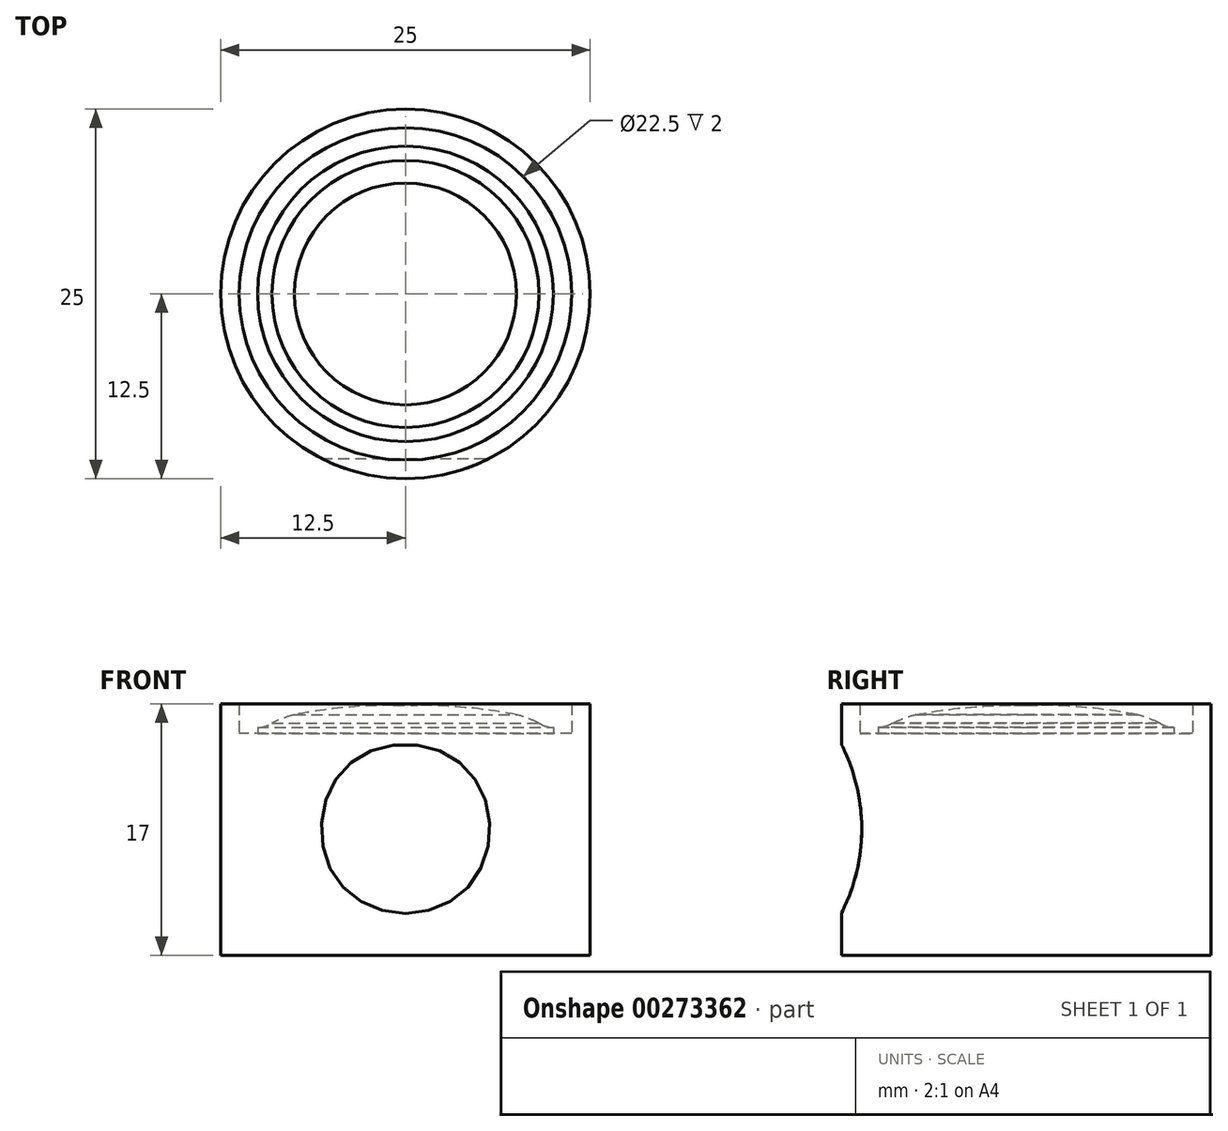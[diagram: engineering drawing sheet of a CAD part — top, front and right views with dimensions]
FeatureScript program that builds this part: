
annotation { "Feature Type Name" : "Feature", "Feature Type Description" : "" }
export const myFeature = defineFeature(function(context is Context, id is Id, definition is map)
    precondition{}
    {
        {
            var Q0;
            Q0=qCreatedBy(makeId("Front.planeOp"),FACE);
            var sketch = newSketch(context, id + "F0", { "sketchPlane" : qUnion([Q0])});
            skLineSegment(sketch, "E0", {"start": v(4.98, -0.38) * mm, "end": v(4.98, 1.12) * mm});
            skLineSegment(sketch, "E1", {"start": v(4.98, 1.12) * mm, "end": v(4.18, 1.12) * mm});
            skLineSegment(sketch, "E2", {"start": v(4.98, -0.38) * mm, "end": v(4.98, -0.79) * mm});
            skLineSegment(sketch, "E3", {"start": v(-6.42, -0.38) * mm, "end": v(-5.02, -0.38) * mm, "construction": true});
            skLineSegment(sketch, "E4", {"start": v(4.98, -0.79) * mm, "end": v(-5.02, -0.79) * mm});
            skLineSegment(sketch, "E5", {"start": v(-5.02, -0.79) * mm, "end": v(-5.02, -0.38) * mm});
            skArc(sketch, "E6", {"start": v(4.18, 1.12) * mm, "mid": v(0.81, 0.96) * mm, "end": v(-2.53, 0.49) * mm});
            skArc(sketch, "E7", {"start": v(-5.02, -0.38) * mm, "mid": v(-4.51, -0.3) * mm, "end": v(-4.05, -0.08) * mm});
            skArc(sketch, "E8", {"start": v(-2.53, 0.49) * mm, "mid": v(-3.3, 0.24) * mm, "end": v(-4.05, -0.08) * mm});
            skSolve(sketch);
        }
        {
            var Q0;
            Q0=makeQuery(id+"F0.imprint","IMPRINT",FACE,{"disambiguationData":[TD([[makeQuery(id+"F0.imprint","IMPRINT",EDGE,{"derivedFrom":sQuery(id+"F0.wireOp",EDGE,"E0")}),1.0]])]});
            var Q1;
            Q1=sQuery(id+"F0.wireOp",EDGE,"E0");
            revolve(context, id + "F1", {"entities" : qUnion([Q0]), "axis" : qUnion([Q1]), "revolveType" : RevolveType.FULL});
        }
        {
            var Q0;
            Q0=makeQuery(id+"F1.opRevolve","SWEPT_FACE",FACE,{"disambiguationData":[OSD([sQuery(id+"F0.wireOp",EDGE,"E4")])]});
            var sketch = newSketch(context, id + "F2", { "sketchPlane" : qUnion([Q0])});
            skCircle(sketch, "E9", {"center": v(4.98, 0) * mm, "radius": 12.5 * mm});
            skSolve(sketch);
        }
        {
            var Q0;
            Q0=makeQuery(id+"F2.imprint","IMPRINT",FACE,{"disambiguationData":[TD([[makeQuery(id+"F2.imprint","IMPRINT",EDGE,{"derivedFrom":sQuery(id+"F2.wireOp",EDGE,"E9")}),1.0]])]});
            var Q1;
            Q1=makeQuery(id+"F2.imprint","IMPRINT",FACE,{"disambiguationData":[TD([[makeQuery(id+"F2.imprint","IMPRINT",EDGE,{"derivedFrom":makeQuery(id+"F1.opRevolve","SWEPT_EDGE",EDGE,{"disambiguationData":[OSD([sQuery(id+"F0.wireOp",EDGE,"E4"),sQuery(id+"F0.wireOp",EDGE,"E5")])]})}),1.0]])]});
            extrude(context, id + "F3", {"entities" : qUnion([Q0, Q1]), "operationType" : NewBodyOperationType.ADD, "depth" : 15 * mm, "offsetDistance" : 25 * mm});
        }
        {
            var Q0;
            Q0=makeQuery(id+"F3.opExtrude","CAP_FACE",FACE,{"disambiguationData":[OSD([sQuery(id+"F2.wireOp",EDGE,"E9")])],"isStart":true});
            var sketch = newSketch(context, id + "F4", { "sketchPlane" : qUnion([Q0])});
            skCircle(sketch, "E10", {"center": v(4.98, 0) * mm, "radius": 11.25 * mm});
            skSolve(sketch);
        }
        {
            var Q0;
            Q0=makeQuery(id+"F4.imprint","IMPRINT",FACE,{"disambiguationData":[TD([[makeQuery(id+"F4.imprint","IMPRINT",EDGE,{"derivedFrom":sQuery(id+"F4.wireOp",EDGE,"E10")}),-1.0]])]});
            extrude(context, id + "F5", {"entities" : qUnion([Q0]), "operationType" : NewBodyOperationType.ADD, "depth" : 2 * mm, "offsetDistance" : 25 * mm});
        }
        {
            var Q0;
            Q0=qCreatedBy(makeId("Right.planeOp"),FACE);
            cPlane(context, id + "F6", {"entities" : qUnion([Q0]), "cplaneType" : CPlaneType.OFFSET, "offset" : 17.3 * mm, "width" : 150 * mm, "height" : 150 * mm});
        }
        {
            var Q0;
            Q0=qCreatedBy(id+"F6.planeOp",FACE);
            var sketch = newSketch(context, id + "F7", { "sketchPlane" : qUnion([Q0])});
            skLineSegment(sketch, "E11", {"start": v(-13.47, 2.71) * mm, "end": v(0, 2.71) * mm, "construction": true});
            skLineSegment(sketch, "E12", {"start": v(0, 1.27) * mm, "end": v(0, -15.75) * mm, "construction": true});
            skLineSegment(sketch, "E13", {"start": v(0, -7.24) * mm, "end": v(-13.25, -7.24) * mm, "construction": true});
            skPoint(sketch, "E13.endSnap0", {"position": v(0, -7.24) * mm});
            skArc(sketch, "E14", {"start": v(-13.25, -14.24) * mm, "mid": v(-11.12, -7.24) * mm, "end": v(-13.25, -0.24) * mm});
            skArc(sketch, "E15.MirrorCS", {"start": v(13.25, -14.24) * mm, "mid": v(11.12, -7.24) * mm, "end": v(13.25, -0.24) * mm});
            skLineSegment(sketch, "E16", {"start": v(-13.25, -0.24) * mm, "end": v(-13.25, -14.24) * mm});
            skLineSegment(sketch, "E17.MirrorCS", {"start": v(13.25, -7.24) * mm, "end": v(13.25, -0.24) * mm, "construction": true});
            skLineSegment(sketch, "E18.MirrorCS", {"start": v(13.25, -7.24) * mm, "end": v(13.25, -14.24) * mm, "construction": true});
            skLineSegment(sketch, "E19.MirrorCS", {"start": v(13.25, -0.24) * mm, "end": v(13.25, -14.24) * mm});
            skSolve(sketch);
        }
        {
            var Q0;
            Q0=makeQuery(id+"F7.imprint","IMPRINT",FACE,{"disambiguationData":[TD([[makeQuery(id+"F7.imprint","IMPRINT",EDGE,{"derivedFrom":sQuery(id+"F7.wireOp",EDGE,"E14")}),1.0]])]});
            var Q1;
            Q1=makeQuery(id+"F7.imprint","IMPRINT",FACE,{"disambiguationData":[TD([[makeQuery(id+"F7.imprint","IMPRINT",EDGE,{"derivedFrom":sQuery(id+"F7.wireOp",EDGE,"E15.MirrorCS")}),-1.0]])]});
            extrude(context, id + "F8", {"entities" : qUnion([Q0, Q1]), "operationType" : NewBodyOperationType.REMOVE, "oppositeDirection" : true, "depth" : 50 * mm, "offsetDistance" : 25 * mm});
        }
    });
